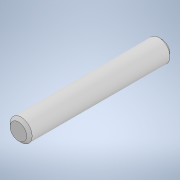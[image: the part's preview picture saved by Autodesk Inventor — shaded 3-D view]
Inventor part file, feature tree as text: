
AUTODESK INVENTOR PART (.ipt)
format: ipt  version: 2020.2 (Build 242310000, 310)  size: 96,768 bytes
history: native  units: mm
features: extrude x1, chamfer x1, sketch x1
ambient origin geometry x8: Origin, YZ Plane, XZ Plane, XY Plane, X Axis, Y Axis, Z Axis, Center Point
bodies: Solid1 (feature_tree)
feature tree (3):
  extrude  "Extrusion1"  Depth=13.0mm TaperAngle=0.0deg
  chamfer  "Chamfer1"  Distance=0.25mm Angle=45.0deg
  sketch  "Sketch1"  dims[d0=2.0mm d1=13.0mm d2=0.0mm d3=0.25mm d4=2.0mm d5=45.0deg]
